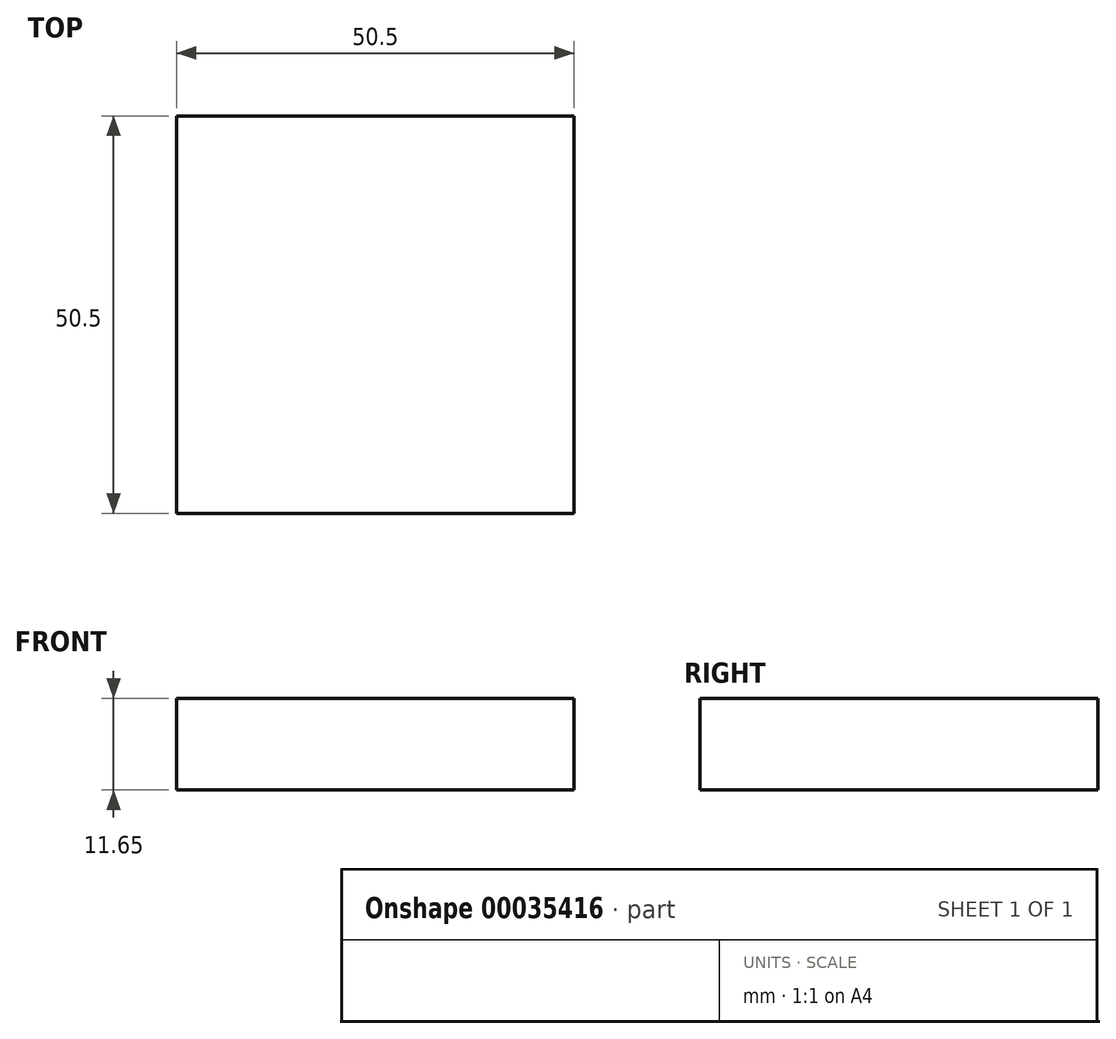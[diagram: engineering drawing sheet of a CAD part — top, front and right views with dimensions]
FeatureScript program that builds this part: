
annotation { "Feature Type Name" : "Feature", "Feature Type Description" : "" }
export const myFeature = defineFeature(function(context is Context, id is Id, definition is map)
    precondition{}
    {
        {
            var Q0;
            Q0=qCreatedBy(makeId("Top.planeOp"),FACE);
            var sketch = newSketch(context, id + "F0", { "sketchPlane" : qUnion([Q0])});
            skLineSegment(sketch, "E0.rect.bottom", {"start": v(-23.5, 25.25) * mm, "end": v(27, 25.25) * mm});
            skLineSegment(sketch, "E0.rect.top", {"start": v(-23.5, -25.25) * mm, "end": v(27, -25.25) * mm});
            skLineSegment(sketch, "E0.rect.left", {"start": v(-23.5, 25.25) * mm, "end": v(-23.5, -25.25) * mm});
            skLineSegment(sketch, "E0.rect.right", {"start": v(27, 25.25) * mm, "end": v(27, -25.25) * mm});
            skPoint(sketch, "E0.rect.middle", {"position": v(1.75, 0) * mm});
            skSolve(sketch);
        }
        {
            var Q0;
            Q0=makeQuery(id+"F0.imprint","IMPRINT",FACE,{"disambiguationData":[TD([[makeQuery(id+"F0.imprint","IMPRINT",EDGE,{"derivedFrom":sQuery(id+"F0.wireOp",EDGE,"E0.rect.bottom")}),-1.0]])]});
            extrude(context, id + "F1", {"entities" : qUnion([Q0]), "oppositeDirection" : true, "depth" : 11.65 * mm});
        }
    });
